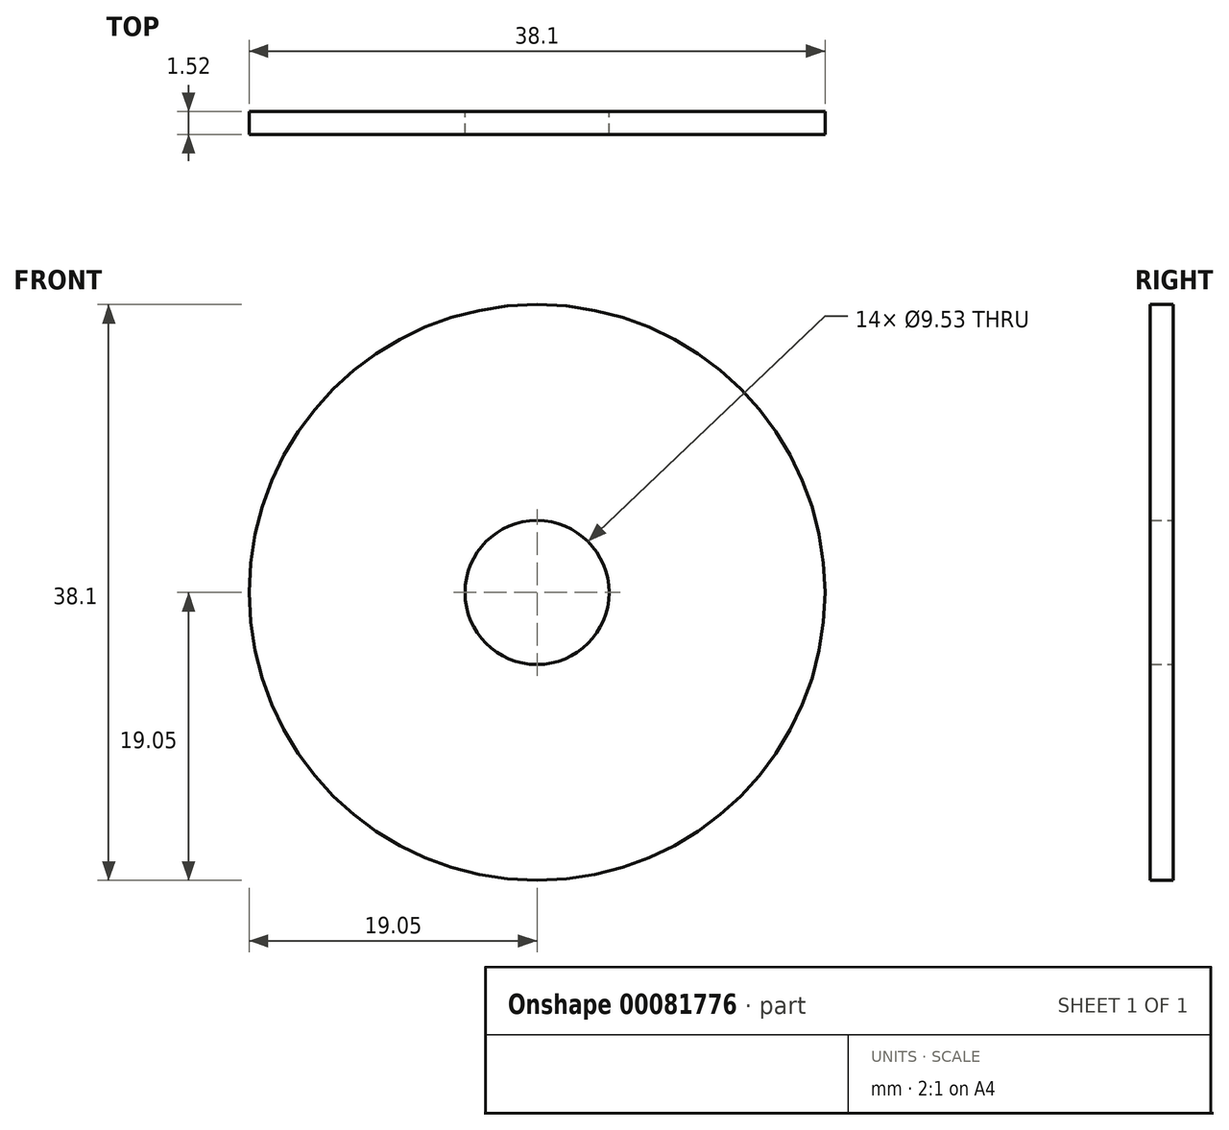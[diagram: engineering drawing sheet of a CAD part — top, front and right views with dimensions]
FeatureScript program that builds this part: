
annotation { "Feature Type Name" : "Feature", "Feature Type Description" : "" }
export const myFeature = defineFeature(function(context is Context, id is Id, definition is map)
    precondition{}
    {
        {
            var Q0;
            Q0=qCreatedBy(makeId("Front.planeOp"),FACE);
            var sketch = newSketch(context, id + "F0", { "sketchPlane" : qUnion([Q0])});
            skCircle(sketch, "E0", {"center": v(0, 0) * mm, "radius": 4.76 * mm});
            skCircle(sketch, "E1", {"center": v(0, 0) * mm, "radius": 19.05 * mm});
            skSolve(sketch);
        }
        {
            var Q0;
            Q0=makeQuery(id+"F0.imprint","IMPRINT",FACE,{"disambiguationData":[TD([[makeQuery(id+"F0.imprint","IMPRINT",EDGE,{"derivedFrom":sQuery(id+"F0.wireOp",EDGE,"E0")}),-1.0]])]});
            extrude(context, id + "F1", {"entities" : qUnion([Q0]), "depth" : 1.52 * mm});
        }
    });
